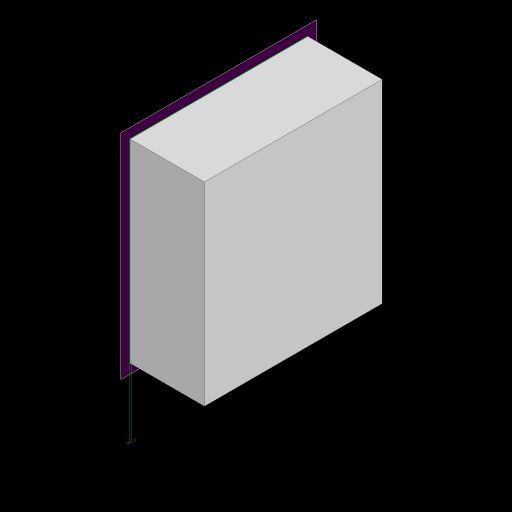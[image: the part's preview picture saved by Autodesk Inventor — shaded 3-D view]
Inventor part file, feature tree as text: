
AUTODESK INVENTOR PART (.ipt)
format: ipt  version: 2023 (Build 270158000, 158)  size: 396,800 bytes
history: native  units: in
note: dims shown in document units (in); Inventor stores cm internally (conversion verified against a paired STEP export)
features: sketch x10, extrude x9, projected_geometry x5, plane x2, fillet x2, split x1
ambient origin geometry x8: Origin, YZ Plane, XZ Plane, XY Plane, X Axis, Y Axis, Z Axis, Center Point
bodies: Solid1 (feature_tree)
feature tree (29):
  extrude  "Extrusion1"  Depth=3.937in
  sketch  "Sketch2"  dims[d2=5.1181in d3=0.0in d4=0.315in d5=0.0in]
  extrude  "Extrusion2"  Depth=0.315in TaperAngle=0.0deg
  extrude  "Extrusion3"  Depth=3.937in
  plane  "Work Plane1"
  extrude  "Extrusion4"  Depth=5.1181in
  fillet  "Fillet1"  Radius=5.1181in
  sketch  "Sketch8"  dims[d8=1.9685in d9=2.5591in d10=5.1181in]
  extrude  "Extrusion10"  Depth=0.1496in
  extrude  "Extrusion11"  [1 undecoded]
  fillet  "Fillet2"  Radius=0.1969in
  extrude  "Extrusion12"  Depth=0.1969in
  extrude  "Extrusion13"  Depth=3.5433in TaperAngle=0.0deg
  extrude  "Extrusion14"  Depth=0.1969in TaperAngle=0.0deg
  plane  "Work Plane2"
  split  "Split1"
  sketch  "Sketch18"  dims[d82=4.685in d84=5.0in d85=0.0in d86=0.1969in d87=45.0deg d88=45.0deg d90=45.0deg d91=45.0deg d92=0.7874in d93=0.9843in d94=0.7874in d95=0.9843in d96=0.0394in d97=3.3465in d98=4.3307in d99=3.5433in d100=0.0984in d101=0.1575in d102=0.1693in d103=0.1417in d104=0.1969in d105=0.1693in d107=4.7244in d108=0.1969in d109=0.1575in d110=0.1417in d111=0.1969in d112=0.1417in d113=0.1969in d114=0.1417in d115=0.1969in d116=0.1181in d117=0.0in d118=0.7087in d119=0.1181in d121=0.7087in d122=1.3386in d123=0.7874in d124=0.0in d125=45.0deg d126=2.874in d129=3.5433in d130=0.1673in d131=0.1417in d135=0.1417in d136=0.1417in d137=0.1417in d138=1.5748in d139=0.0in d140=0.0512in]
  sketch  "Sketch1"  dims[d0=4.685in d1=3.937in]
  sketch  "Sketch3"  dims[d6=3.5433in d7=3.937in]
  projected_geometry  "Projected Loop1"
  sketch  "Sketch10"  dims[d11=2.874in d12=0.1496in]
  projected_geometry  "Projected Loop2"
  sketch  "Sketch12"  dims[d13=0.7087in d14=0.0in d15=-0.1969in d16=0.1969in]
  projected_geometry  "Projected Loop4"
  sketch  "Sketch13"  dims[d17=0.1969in d18=0.1969in]
  sketch  "Sketch14"  dims[d19=3.5433in d20=0.0in d21=3.5433in d22=0.0in]
  sketch  "Sketch15"  dims[d23=0.1969in d74=0.1969in d75=0.0in]
  projected_geometry  "Projected Loop5"
  projected_geometry  "Project Cut Edges1"
note: 1 required parameter value undecoded (feature->parameter linkage not recoverable at this tier; creation-order binding heuristic only, values carry confidence <= 0.55)
